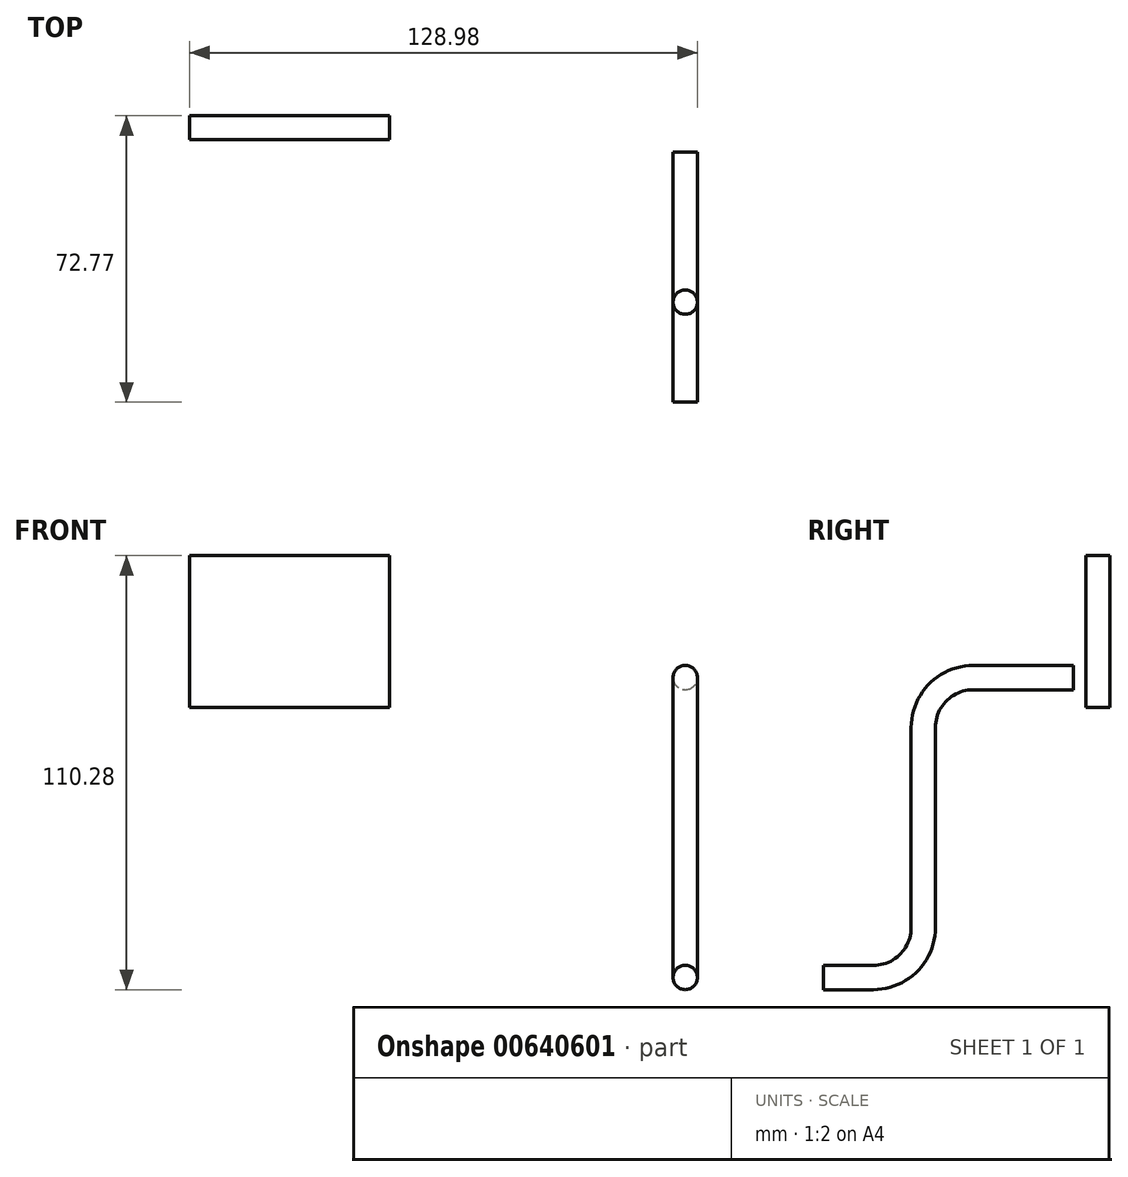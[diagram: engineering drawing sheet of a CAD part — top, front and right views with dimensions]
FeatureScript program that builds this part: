
annotation { "Feature Type Name" : "Feature", "Feature Type Description" : "" }
export const myFeature = defineFeature(function(context is Context, id is Id, definition is map)
    precondition{}
    {
        {
            var Q0;
            Q0=qCreatedBy(makeId("Right.planeOp"),FACE);
            var sketch = newSketch(context, id + "F0", { "sketchPlane" : qUnion([Q0])});
            skLineSegment(sketch, "E0", {"start": v(0, 0) * mm, "end": v(-25.4, 0) * mm});
            skLineSegment(sketch, "E1", {"start": v(-38.1, -12.7) * mm, "end": v(-38.1, -63.5) * mm});
            skLineSegment(sketch, "E2", {"start": v(-50.8, -76.2) * mm, "end": v(-63.5, -76.2) * mm});
            skPoint(sketch, "E3.visualSharp", {"position": v(-38.1, 0) * mm});
            skArc(sketch, "E3.filletArc", {"start": v(-25.4, 0) * mm, "mid": v(-34.38, -3.72) * mm, "end": v(-38.1, -12.7) * mm});
            skPoint(sketch, "E4.visualSharp", {"position": v(-38.1, -76.2) * mm});
            skArc(sketch, "E4.filletArc", {"start": v(-50.8, -76.2) * mm, "mid": v(-41.82, -72.48) * mm, "end": v(-38.1, -63.5) * mm});
            skSolve(sketch);
        }
        {
            var Q0;
            Q0=qCreatedBy(makeId("Front.planeOp"),FACE);
            var sketch = newSketch(context, id + "F1", { "sketchPlane" : qUnion([Q0])});
            skCircle(sketch, "E5", {"center": v(0, 0) * mm, "radius": 3.09 * mm});
            skSolve(sketch);
        }
        {
            var Q0;
            Q0=makeQuery(id+"F1.imprint","IMPRINT",FACE,{"disambiguationData":[TD([[makeQuery(id+"F1.imprint","IMPRINT",EDGE,{"derivedFrom":sQuery(id+"F1.wireOp",EDGE,"E5")}),1.0]])]});
            var Q1;
            Q1=sQuery(id+"F0.wireOp",EDGE,"E0");
            var Q2;
            Q2=sQuery(id+"F0.wireOp",EDGE,"E3.filletArc");
            var Q3;
            Q3=sQuery(id+"F0.wireOp",EDGE,"E1");
            var Q4;
            Q4=sQuery(id+"F0.wireOp",EDGE,"E4.filletArc");
            var Q5;
            Q5=sQuery(id+"F0.wireOp",EDGE,"E2");
            sweep(context, id + "F2", {"profiles" : qUnion([Q0]), "path" : qUnion([Q1, Q2, Q3, Q4, Q5])});
        }
        {
            var Q0;
            Q0=qCreatedBy(makeId("Top.planeOp"),FACE);
            var sketch = newSketch(context, id + "F3", { "sketchPlane" : qUnion([Q0])});
            skLineSegment(sketch, "E6.bottom", {"start": v(-125.9, 9.27) * mm, "end": v(-75.1, 9.27) * mm});
            skLineSegment(sketch, "E6.top", {"start": v(-125.9, 3.15) * mm, "end": v(-75.1, 3.15) * mm});
            skLineSegment(sketch, "E6.left", {"start": v(-125.9, 9.27) * mm, "end": v(-125.9, 3.15) * mm});
            skLineSegment(sketch, "E6.right", {"start": v(-75.1, 9.27) * mm, "end": v(-75.1, 3.15) * mm});
            skSolve(sketch);
        }
        {
            var Q0;
            Q0=makeQuery(id+"F3.imprint","IMPRINT",FACE,{"disambiguationData":[TD([[makeQuery(id+"F3.imprint","IMPRINT",EDGE,{"derivedFrom":sQuery(id+"F3.wireOp",EDGE,"E6.bottom")}),-1.0]])]});
            extrude(context, id + "F4", {"entities" : qUnion([Q0]), "depth" : 30.99 * mm, "offsetDistance" : 25.4 * mm});
        }
        {
            var Q0;
            Q0=makeQuery(id+"F4.opExtrude","CAP_FACE",FACE,{"disambiguationData":[OSD([sQuery(id+"F3.wireOp",EDGE,"E6.bottom"),sQuery(id+"F3.wireOp",EDGE,"E6.top"),sQuery(id+"F3.wireOp",EDGE,"E6.left"),sQuery(id+"F3.wireOp",EDGE,"E6.right")])],"isStart":true});
            extrude(context, id + "F5", {"entities" : qUnion([Q0]), "operationType" : NewBodyOperationType.ADD, "depth" : 7.62 * mm, "offsetDistance" : 25.4 * mm});
        }
    });
